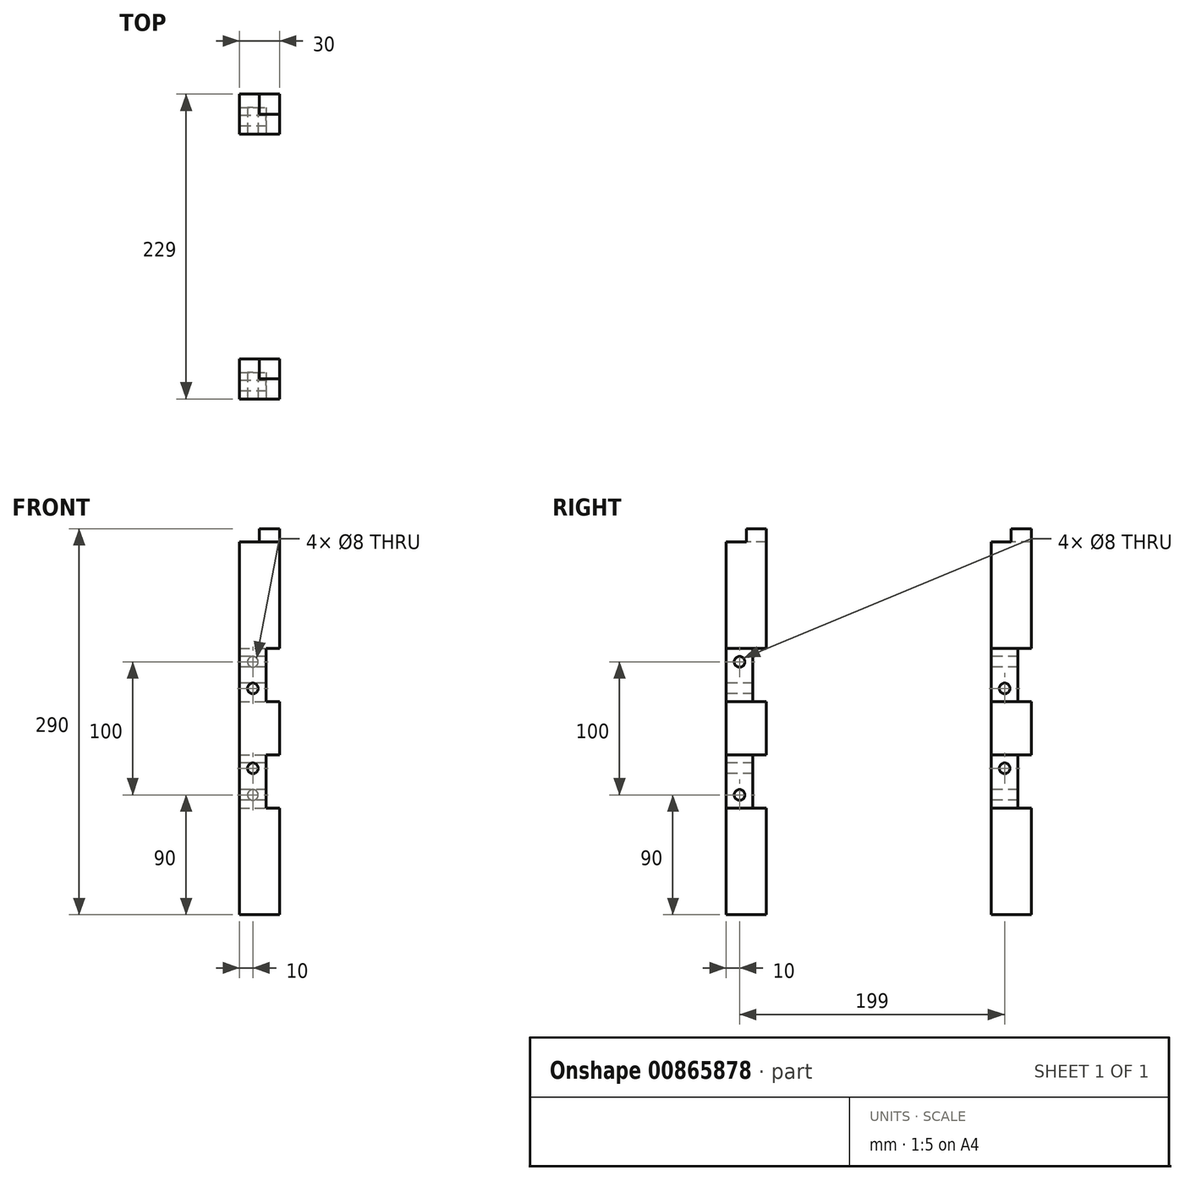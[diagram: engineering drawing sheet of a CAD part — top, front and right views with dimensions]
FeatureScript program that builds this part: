
annotation { "Feature Type Name" : "Feature", "Feature Type Description" : "" }
export const myFeature = defineFeature(function(context is Context, id is Id, definition is map)
    precondition{}
    {
        {
            var Q0;
            Q0=qCreatedBy(makeId("Top.planeOp"),FACE);
            var sketch = newSketch(context, id + "F0", { "sketchPlane" : qUnion([Q0])});
            skLineSegment(sketch, "E0.bottom", {"start": v(0, 0) * mm, "end": v(30, 0) * mm});
            skLineSegment(sketch, "E0.top", {"start": v(0, 30) * mm, "end": v(30, 30) * mm});
            skLineSegment(sketch, "E0.left", {"start": v(0, 0) * mm, "end": v(0, 30) * mm});
            skLineSegment(sketch, "E0.right", {"start": v(30, 0) * mm, "end": v(30, 30) * mm});
            skSolve(sketch);
        }
        {
            var Q0;
            Q0 = qSketchRegion(id + "F0", true);
            extrude(context, id + "F1", {"entities" : qUnion([Q0]), "depth" : 280 * mm, "offsetDistance" : 25 * mm});
        }
        {
            var Q0;
            Q0=makeQuery(id+"F1.opExtrude","CAP_FACE",FACE,{"disambiguationData":[OSD([sQuery(id+"F0.wireOp",EDGE,"E0.bottom"),sQuery(id+"F0.wireOp",EDGE,"E0.top"),sQuery(id+"F0.wireOp",EDGE,"E0.left"),sQuery(id+"F0.wireOp",EDGE,"E0.right")])],"isStart":false});
            var sketch = newSketch(context, id + "F2", { "sketchPlane" : qUnion([Q0])});
            skPoint(sketch, "E1.oppositeSnap0", {"position": v(30, 15) * mm});
            skLineSegment(sketch, "E1.bottom", {"start": v(30, 30) * mm, "end": v(15, 30) * mm});
            skLineSegment(sketch, "E1.top", {"start": v(30, 15) * mm, "end": v(15, 15) * mm});
            skLineSegment(sketch, "E1.left", {"start": v(30, 30) * mm, "end": v(30, 15) * mm});
            skLineSegment(sketch, "E1.right", {"start": v(15, 30) * mm, "end": v(15, 15) * mm});
            skSolve(sketch);
        }
        {
            var Q0;
            Q0 = qSketchRegion(id + "F2", true);
            extrude(context, id + "F3", {"entities" : qUnion([Q0]), "operationType" : NewBodyOperationType.ADD, "depth" : 10 * mm, "offsetDistance" : 25 * mm});
        }
        {
            var Q0;
            Q0=makeQuery(id+"F3.boolean.opBoolean","MERGE",FACE,{"derivedFrom":[makeQuery(id+"F1.opExtrude","SWEPT_FACE",FACE,{"disambiguationData":[OSD([sQuery(id+"F0.wireOp",EDGE,"E0.top")])]}),makeQuery(id+"F3.opExtrude","SWEPT_FACE",FACE,{"disambiguationData":[OSD([sQuery(id+"F2.wireOp",EDGE,"E1.bottom")])]})]});
            var sketch = newSketch(context, id + "F4", { "sketchPlane" : qUnion([Q0])});
            skLineSegment(sketch, "E2.bottom", {"start": v(0, 200) * mm, "end": v(-30, 200) * mm});
            skLineSegment(sketch, "E2.top", {"start": v(0, 160) * mm, "end": v(-30, 160) * mm});
            skLineSegment(sketch, "E2.left", {"start": v(0, 200) * mm, "end": v(0, 160) * mm});
            skLineSegment(sketch, "E2.right", {"start": v(-30, 200) * mm, "end": v(-30, 160) * mm});
            skLineSegment(sketch, "E3.bottom", {"start": v(0, 120) * mm, "end": v(-30, 120) * mm});
            skLineSegment(sketch, "E3.top", {"start": v(0, 80) * mm, "end": v(-30, 80) * mm});
            skLineSegment(sketch, "E3.left", {"start": v(0, 120) * mm, "end": v(0, 80) * mm});
            skLineSegment(sketch, "E3.right", {"start": v(-30, 120) * mm, "end": v(-30, 80) * mm});
            skSolve(sketch);
        }
        {
            var Q0;
            Q0 = qSketchRegion(id + "F4", true);
            extrude(context, id + "F5", {"entities" : qUnion([Q0]), "operationType" : NewBodyOperationType.REMOVE, "oppositeDirection" : true, "depth" : 10 * mm, "offsetDistance" : 25 * mm});
        }
        {
            var Q0;
            Q0=makeQuery(id+"F3.boolean.opBoolean","MERGE",FACE,{"derivedFrom":[makeQuery(id+"F1.opExtrude","SWEPT_FACE",FACE,{"disambiguationData":[OSD([sQuery(id+"F0.wireOp",EDGE,"E0.right")])]}),makeQuery(id+"F3.opExtrude","SWEPT_FACE",FACE,{"disambiguationData":[OSD([sQuery(id+"F2.wireOp",EDGE,"E1.left")])]})]});
            var sketch = newSketch(context, id + "F6", { "sketchPlane" : qUnion([Q0])});
            skLineSegment(sketch, "E4.bottom", {"start": v(20, 200) * mm, "end": v(0, 200) * mm});
            skLineSegment(sketch, "E4.top", {"start": v(20, 160) * mm, "end": v(0, 160) * mm});
            skLineSegment(sketch, "E4.left", {"start": v(20, 200) * mm, "end": v(20, 160) * mm});
            skLineSegment(sketch, "E4.right", {"start": v(0, 200) * mm, "end": v(0, 160) * mm});
            skLineSegment(sketch, "E5.bottom", {"start": v(20, 120) * mm, "end": v(0, 120) * mm});
            skLineSegment(sketch, "E5.top", {"start": v(20, 80) * mm, "end": v(0, 80) * mm});
            skLineSegment(sketch, "E5.left", {"start": v(20, 120) * mm, "end": v(20, 80) * mm});
            skLineSegment(sketch, "E5.right", {"start": v(0, 120) * mm, "end": v(0, 80) * mm});
            skSolve(sketch);
        }
        {
            var Q0;
            Q0 = qSketchRegion(id + "F6", true);
            extrude(context, id + "F7", {"entities" : qUnion([Q0]), "operationType" : NewBodyOperationType.REMOVE, "oppositeDirection" : true, "depth" : 10 * mm, "offsetDistance" : 25 * mm});
        }
        {
            var Q0;
            Q0=makeQuery(id+"F1.opExtrude","SWEPT_BODY",BODY,{"disambiguationData":[OSD([sQuery(id+"F0.wireOp",EDGE,"E0.bottom"),sQuery(id+"F0.wireOp",EDGE,"E0.top"),sQuery(id+"F0.wireOp",EDGE,"E0.left"),sQuery(id+"F0.wireOp",EDGE,"E0.right")])]});
            transform(context, id + "F8", {"entities" : qUnion([Q0]), "transformType" : TransformType.TRANSLATION_3D, "dx" : 0 * mm, "dy" : -199 * mm, "dz" : 0 * mm, "makeCopy" : true});
        }
        {
            var Q0;
            Q0=makeQuery(id+"F1.opExtrude","SWEPT_FACE",FACE,{"disambiguationData":[OSD([sQuery(id+"F0.wireOp",EDGE,"E0.bottom")])]});
            var sketch = newSketch(context, id + "F9", { "sketchPlane" : qUnion([Q0])});
            skCircle(sketch, "E6", {"center": v(10, 190) * mm, "radius": 4 * mm});
            skCircle(sketch, "E7", {"center": v(10, 90) * mm, "radius": 4 * mm});
            skSolve(sketch);
        }
        {
            var Q0;
            Q0 = qSketchRegion(id + "F9", true);
            extrude(context, id + "F10", {"entities" : qUnion([Q0]), "operationType" : NewBodyOperationType.REMOVE, "endBound" : BoundingType.THROUGH_ALL, "oppositeDirection" : true, "depth" : 25 * mm, "offsetDistance" : 25 * mm});
        }
        {
            var Q0;
            Q0=makeQuery(id+"F1.opExtrude","SWEPT_FACE",FACE,{"disambiguationData":[OSD([sQuery(id+"F0.wireOp",EDGE,"E0.left")])]});
            var sketch = newSketch(context, id + "F11", { "sketchPlane" : qUnion([Q0])});
            skCircle(sketch, "E8", {"center": v(-10, 110) * mm, "radius": 4 * mm});
            skCircle(sketch, "E9", {"center": v(-10, 170) * mm, "radius": 4 * mm});
            skSolve(sketch);
        }
        {
            var Q0;
            Q0 = qSketchRegion(id + "F11", true);
            extrude(context, id + "F12", {"entities" : qUnion([Q0]), "operationType" : NewBodyOperationType.REMOVE, "endBound" : BoundingType.THROUGH_ALL, "oppositeDirection" : true, "depth" : 25 * mm, "offsetDistance" : 25 * mm});
        }
        {
            var Q0;
            Q0=makeQuery(id+"F8.opPattern","COPY",FACE,{"derivedFrom":makeQuery(id+"F1.opExtrude","SWEPT_FACE",FACE,{"disambiguationData":[OSD([sQuery(id+"F0.wireOp",EDGE,"E0.bottom")])]}),"instanceName":"1"});
            var sketch = newSketch(context, id + "F13", { "sketchPlane" : qUnion([Q0])});
            skCircle(sketch, "E10", {"center": v(10, 170) * mm, "radius": 4 * mm});
            skCircle(sketch, "E11", {"center": v(10, 110) * mm, "radius": 4 * mm});
            skSolve(sketch);
        }
        {
            var Q0;
            Q0 = qSketchRegion(id + "F13", true);
            extrude(context, id + "F14", {"entities" : qUnion([Q0]), "operationType" : NewBodyOperationType.REMOVE, "oppositeDirection" : true, "depth" : 25 * mm, "offsetDistance" : 25 * mm});
        }
        {
            var Q0;
            Q0=makeQuery(id+"F8.opPattern","COPY",FACE,{"derivedFrom":makeQuery(id+"F1.opExtrude","SWEPT_FACE",FACE,{"disambiguationData":[OSD([sQuery(id+"F0.wireOp",EDGE,"E0.left")])]}),"instanceName":"1"});
            var sketch = newSketch(context, id + "F15", { "sketchPlane" : qUnion([Q0])});
            skCircle(sketch, "E12", {"center": v(189, 190) * mm, "radius": 4 * mm});
            skCircle(sketch, "E13", {"center": v(189, 90) * mm, "radius": 4 * mm});
            skSolve(sketch);
        }
        {
            var Q0;
            Q0 = qSketchRegion(id + "F15", true);
            extrude(context, id + "F16", {"entities" : qUnion([Q0]), "operationType" : NewBodyOperationType.REMOVE, "oppositeDirection" : true, "depth" : 25 * mm, "offsetDistance" : 25 * mm});
        }
    });
